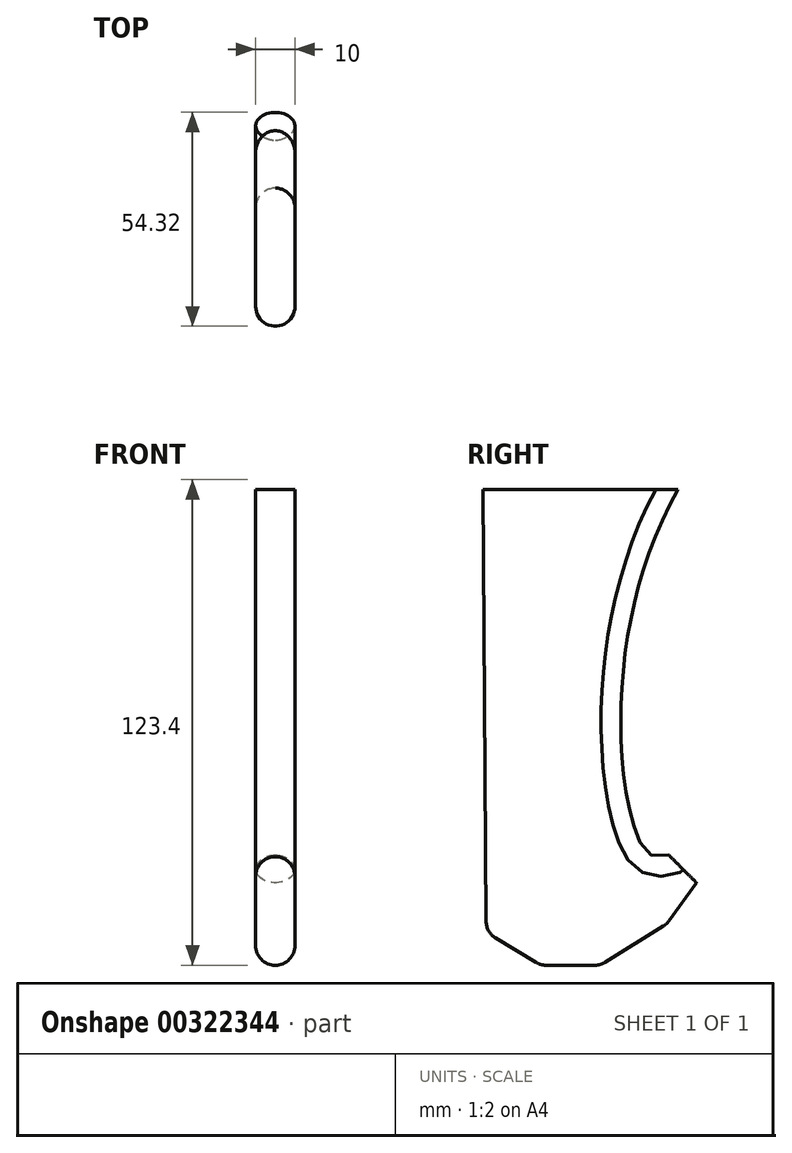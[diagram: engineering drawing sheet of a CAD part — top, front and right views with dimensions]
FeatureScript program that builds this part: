
annotation { "Feature Type Name" : "Feature", "Feature Type Description" : "" }
export const myFeature = defineFeature(function(context is Context, id is Id, definition is map)
    precondition{}
    {
        {
            var Q0;
            Q0=qCreatedBy(makeId("Top.planeOp"),FACE);
            var sketch = newSketch(context, id + "F0", { "sketchPlane" : qUnion([Q0])});
            skLineSegment(sketch, "E0.bottom", {"start": v(50, 50) * mm, "end": v(-50, 50) * mm});
            skLineSegment(sketch, "E0.top", {"start": v(50, -50) * mm, "end": v(-50, -50) * mm});
            skLineSegment(sketch, "E0.left", {"start": v(50, 50) * mm, "end": v(50, -50) * mm});
            skLineSegment(sketch, "E0.right", {"start": v(-50, 50) * mm, "end": v(-50, -50) * mm});
            skPoint(sketch, "E0.middle", {"position": v(0, 0) * mm});
            skSolve(sketch);
        }
        {
            var Q0;
            Q0=qCreatedBy(makeId("Right.planeOp"),FACE);
            var sketch = newSketch(context, id + "F1", { "sketchPlane" : qUnion([Q0])});
            skLineSegment(sketch, "E1", {"start": v(32.93, -92.93) * mm, "end": v(40, -100) * mm});
            skLineSegment(sketch, "E2", {"start": v(40, -100) * mm, "end": v(50, -100) * mm});
            skLineSegment(sketch, "E3", {"start": v(50, -100) * mm, "end": v(50, 0) * mm});
            skLineSegment(sketch, "E4", {"start": v(40, -100) * mm, "end": v(32.42, -110.44) * mm});
            skLineSegment(sketch, "E5", {"start": v(32.42, -110.44) * mm, "end": v(15.56, -120.94) * mm});
            skLineSegment(sketch, "E6", {"start": v(15.56, -120.94) * mm, "end": v(0.42, -120.94) * mm});
            skLineSegment(sketch, "E7", {"start": v(0.42, -120.94) * mm, "end": v(-13.45, -112.58) * mm});
            skLineSegment(sketch, "E8", {"start": v(-13.45, -112.58) * mm, "end": v(-13.84, -53.79) * mm});
            skLineSegment(sketch, "E9", {"start": v(-13.84, -53.79) * mm, "end": v(-14.32, 0) * mm});
            skFitSpline(sketch, "E10", {"points": [v(32.93, -92.93) * mm, v(25.29, -88.96) * mm, v(35.31, 0) * mm], "startDerivative": vector(-48.83, -14.77) * mm, "endDerivative": vector(75.93, 133.53) * mm});
            skLineSegment(sketch, "E11", {"start": v(35.31, 0) * mm, "end": v(-14.32, 0) * mm});
            skSolve(sketch);
        }
        {
            var Q0;
            Q0=makeQuery(id+"F1.imprint","IMPRINT",FACE,{"disambiguationData":[TD([[makeQuery(id+"F1.imprint","IMPRINT",EDGE,{"derivedFrom":sQuery(id+"F1.wireOp",EDGE,"E1")}),-1.0]])]});
            extrude(context, id + "F2", {"entities" : qUnion([Q0]), "endBound" : BoundingType.SYMMETRIC, "depth" : 10 * mm});
        }
        {
            var Q0;
            Q0=makeQuery(id+"F2.opExtrude","CAP_EDGE",EDGE,{"disambiguationData":[OSD([sQuery(id+"F1.wireOp",EDGE,"E8")])],"isStart":false});
            var Q1;
            Q1=makeQuery(id+"F2.opExtrude","CAP_EDGE",EDGE,{"disambiguationData":[OSD([sQuery(id+"F1.wireOp",EDGE,"E7")])],"isStart":false});
            var Q2;
            Q2=makeQuery(id+"F2.opExtrude","CAP_EDGE",EDGE,{"disambiguationData":[OSD([sQuery(id+"F1.wireOp",EDGE,"E6")])],"isStart":false});
            var Q3;
            Q3=makeQuery(id+"F2.opExtrude","CAP_EDGE",EDGE,{"disambiguationData":[OSD([sQuery(id+"F1.wireOp",EDGE,"E5")])],"isStart":false});
            var Q4;
            Q4=makeQuery(id+"F2.opExtrude","CAP_EDGE",EDGE,{"disambiguationData":[OSD([sQuery(id+"F1.wireOp",EDGE,"E4")])],"isStart":false});
            var Q5;
            Q5=makeQuery(id+"F2.opExtrude","CAP_EDGE",EDGE,{"disambiguationData":[OSD([sQuery(id+"F1.wireOp",EDGE,"E10")])],"isStart":false});
            var Q6;
            Q6=makeQuery(id+"F2.opExtrude","CAP_EDGE",EDGE,{"disambiguationData":[OSD([sQuery(id+"F1.wireOp",EDGE,"E9")])],"isStart":false});
            var Q7;
            Q7=makeQuery(id+"F2.opExtrude","CAP_EDGE",EDGE,{"disambiguationData":[OSD([sQuery(id+"F1.wireOp",EDGE,"E5")])],"isStart":true});
            var Q8;
            Q8=makeQuery(id+"F2.opExtrude","CAP_EDGE",EDGE,{"disambiguationData":[OSD([sQuery(id+"F1.wireOp",EDGE,"E6")])],"isStart":true});
            var Q9;
            Q9=makeQuery(id+"F2.opExtrude","CAP_EDGE",EDGE,{"disambiguationData":[OSD([sQuery(id+"F1.wireOp",EDGE,"E7")])],"isStart":true});
            var Q10;
            Q10=makeQuery(id+"F2.opExtrude","CAP_EDGE",EDGE,{"disambiguationData":[OSD([sQuery(id+"F1.wireOp",EDGE,"E4")])],"isStart":true});
            var Q11;
            Q11=makeQuery(id+"F2.opExtrude","CAP_EDGE",EDGE,{"disambiguationData":[OSD([sQuery(id+"F1.wireOp",EDGE,"E10")])],"isStart":true});
            var Q12;
            Q12=makeQuery(id+"F2.opExtrude","CAP_EDGE",EDGE,{"disambiguationData":[OSD([sQuery(id+"F1.wireOp",EDGE,"E8")])],"isStart":true});
            var Q13;
            Q13=makeQuery(id+"F2.opExtrude","CAP_EDGE",EDGE,{"disambiguationData":[OSD([sQuery(id+"F1.wireOp",EDGE,"E9")])],"isStart":true});
            var Q14;
            Q14=makeQuery(id+"F2.opExtrude","SWEPT_FACE",FACE,{"disambiguationData":[OSD([sQuery(id+"F1.wireOp",EDGE,"E5")])]});
            var Q15;
            Q15=makeQuery(id+"F2.opExtrude","SWEPT_EDGE",EDGE,{"disambiguationData":[OSD([sQuery(id+"F1.wireOp",EDGE,"E6"),sQuery(id+"F1.wireOp",EDGE,"E7")])]});
            var Q16;
            Q16=makeQuery(id+"F2.opExtrude","SWEPT_EDGE",EDGE,{"disambiguationData":[OSD([sQuery(id+"F1.wireOp",EDGE,"E7"),sQuery(id+"F1.wireOp",EDGE,"E8")])]});
            fillet(context, id + "F3", {"entities" : qUnion([Q0, Q1, Q2, Q3, Q4, Q5, Q6, Q7, Q8, Q9, Q10, Q11, Q12, Q13, Q14, Q15, Q16]), "radius" : 5 * mm, "tangentPropagation" : true, "allowEdgeOverflow" : false});
        }
    });
